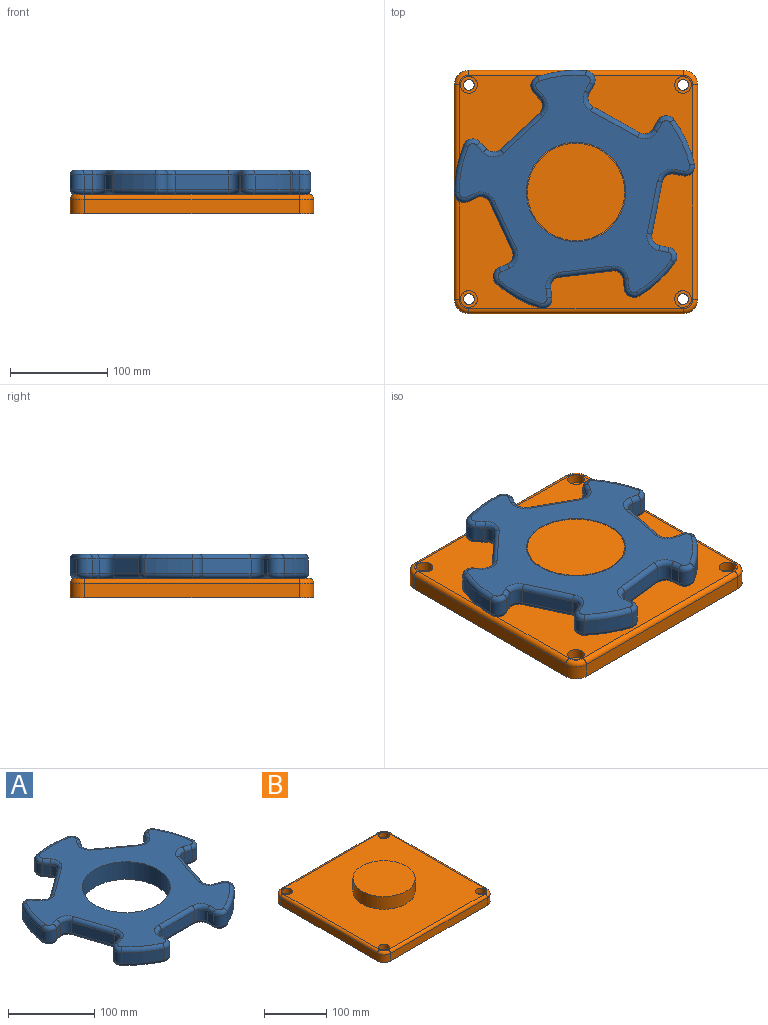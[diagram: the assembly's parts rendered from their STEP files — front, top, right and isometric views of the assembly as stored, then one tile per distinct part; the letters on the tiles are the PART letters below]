
ASSEMBLY  parts=2 mates=1
PART A: 123 faces, bbox 268.9x258.5x25 mm
  f0: plane 238.57x229.73mm, normal (0,0,1), area 21505.7mm2, adj f6,f83,f84,f85,f86,f87,f88,f89
  f1: plane 238.57x229.73mm, normal (0,0,-1), area 21505.7mm2, adj f6,f43,f44,f45,f46,f47,f48,f49
  f2: cylinder r=125mm len=47.82mm, axis (0,0,-1), area 759.5mm2, adj f34,f42,f74,f114
  f3: cylinder r=125mm len=50.29mm, axis (0,0,-1), area 759.5mm2, adj f27,f35,f75,f115
  f4: cylinder r=125mm len=47.82mm, axis (0,0,-1), area 759.5mm2, adj f20,f28,f59,f99
  f5: cylinder r=125mm len=40.68mm, axis (0,0,-1), area 759.5mm2, adj f13,f21,f43,f83
  f6: cylinder r=51mm len=102mm, axis (0,0,-1), area 8011.1mm2, adj f0,f1
  f7: cylinder r=125mm len=40.68mm, axis (0,0,-1), area 759.5mm2, adj f14,f41,f58,f98
  f8: plane 15x9.73mm, normal (-1,0,0), area 146mm2, adj f11,f14,f54,f94
  f9: plane 55x15mm, normal (0,-1,0), area 825mm2, adj f11,f12,f50,f90
  f10: plane 15x9.73mm, normal (1,0,0), area 146mm2, adj f12,f13,f46,f86
  f11: cylinder r=10mm len=15mm, axis (0,0,-1), area 235.6mm2, adj f8,f9,f52,f92
  f12: cylinder r=10mm len=15mm, axis (0,0,-1), area 235.6mm2, adj f9,f10,f48,f88
  f13: cylinder r=10mm len=15mm, axis (0,0,-1), area 299.5mm2, adj f5,f10,f44,f84
  f14: cylinder r=10mm len=15mm, axis (0,0,-1), area 299.5mm2, adj f7,f8,f56,f96
  f15: plane 15x9.26mm, normal (-0.31,0.95,0), area 146mm2, adj f18,f21,f47,f87
  f16: plane 52.31x17mm, normal (-0.95,-0.31,0), area 825mm2, adj f18,f19,f51,f91
  f17: plane 15x9.26mm, normal (0.31,-0.95,0), area 146mm2, adj f19,f20,f55,f95
  f18: cylinder r=10mm len=15mm, axis (0,0,-1), area 235.6mm2, adj f15,f16,f49,f89
  f19: cylinder r=10mm len=15mm, axis (0,0,-1), area 235.6mm2, adj f16,f17,f53,f93
  f20: cylinder r=10mm len=15mm, axis (0,0,-1), area 299.5mm2, adj f4,f17,f57,f97
  f21: cylinder r=10mm len=16.25mm, axis (0,0,-1), area 299.5mm2, adj f5,f15,f45,f85
  f22: plane 15x7.87mm, normal (0.81,0.59,0), area 146mm2, adj f25,f28,f63,f103
  f23: plane 44.5x32.33mm, normal (-0.59,0.81,0), area 825mm2, adj f25,f26,f67,f107
  f24: plane 15x7.87mm, normal (-0.81,-0.59,0), area 146mm2, adj f26,f27,f71,f111
  f25: cylinder r=10mm len=15mm, axis (0,0,-1), area 235.6mm2, adj f22,f23,f65,f105
  f26: cylinder r=10mm len=15mm, axis (0,0,-1), area 235.6mm2, adj f23,f24,f69,f109
  f27: cylinder r=10mm len=15.67mm, axis (0,0,-1), area 299.5mm2, adj f3,f24,f73,f113
  f28: cylinder r=10mm len=16.78mm, axis (0,0,-1), area 299.5mm2, adj f4,f22,f61,f101
  f29: plane 15x7.87mm, normal (0.81,-0.59,0), area 146mm2, adj f32,f35,f79,f119
  f30: plane 44.5x32.33mm, normal (0.59,0.81,0), area 825mm2, adj f32,f33,f82,f122
  f31: plane 15x7.87mm, normal (-0.81,0.59,0), area 146mm2, adj f33,f34,f78,f118
  f32: cylinder r=10mm len=15mm, axis (0,0,-1), area 235.6mm2, adj f29,f30,f81,f121
  f33: cylinder r=10mm len=15mm, axis (0,0,-1), area 235.6mm2, adj f30,f31,f80,f120
  f34: cylinder r=10mm len=16.78mm, axis (0,0,-1), area 299.5mm2, adj f2,f31,f76,f116
  f35: cylinder r=10mm len=15.67mm, axis (0,0,-1), area 299.5mm2, adj f3,f29,f77,f117
  f36: plane 15x9.26mm, normal (-0.31,-0.95,0), area 146mm2, adj f39,f42,f70,f110
  f37: plane 52.31x17mm, normal (0.95,-0.31,0), area 825mm2, adj f39,f40,f66,f106
  f38: plane 15x9.26mm, normal (0.31,0.95,0), area 146mm2, adj f40,f41,f62,f102
  f39: cylinder r=10mm len=15mm, axis (0,0,-1), area 235.6mm2, adj f36,f37,f68,f108
  f40: cylinder r=10mm len=15mm, axis (0,0,-1), area 235.6mm2, adj f37,f38,f64,f104
  f41: cylinder r=10mm len=16.25mm, axis (0,0,-1), area 299.5mm2, adj f7,f38,f60,f100
  f42: cylinder r=10mm len=15mm, axis (0,0,-1), area 299.5mm2, adj f2,f36,f72,f112
  f43: torus R=120mm, axis (0,0,1), area 391.9mm2, adj f1,f5,f44,f45
  f44: torus R=5mm, axis (0,0,1), area 128.3mm2, adj f1,f13,f43,f46
  f45: torus R=5mm, axis (0,0,1), area 128.3mm2, adj f1,f21,f43,f47
  f46: cylinder r=5mm len=9.73mm, axis (0,-1,0), area 76.4mm2, adj f1,f10,f44,f48
  f47: cylinder r=5mm len=10.8mm, axis (0.95,0.31,0), area 76.4mm2, adj f1,f15,f45,f49
  f48: torus R=15mm, axis (0,0,1), area 145.8mm2, adj f1,f12,f46,f50
  f49: torus R=15mm, axis (0,0,1), area 145.8mm2, adj f1,f18,f47,f51
  f50: cylinder r=5mm len=55mm, axis (-1,0,0), area 432mm2, adj f1,f9,f48,f52
  f51: cylinder r=5mm len=53.85mm, axis (-0.31,0.95,0), area 432mm2, adj f1,f16,f49,f53
  f52: torus R=15mm, axis (0,0,1), area 145.8mm2, adj f1,f11,f50,f54
  f53: torus R=15mm, axis (0,0,1), area 145.8mm2, adj f1,f19,f51,f55
  f54: cylinder r=5mm len=9.73mm, axis (0,1,0), area 76.4mm2, adj f1,f8,f52,f56
  f55: cylinder r=5mm len=10.8mm, axis (-0.95,-0.31,0), area 76.4mm2, adj f1,f17,f53,f57
  f56: torus R=5mm, axis (0,0,1), area 128.3mm2, adj f1,f14,f54,f58
  f57: torus R=5mm, axis (0,0,1), area 128.3mm2, adj f1,f20,f55,f59
  f58: torus R=120mm, axis (0,0,1), area 391.9mm2, adj f1,f7,f56,f60
  f59: torus R=120mm, axis (0,0,1), area 391.9mm2, adj f1,f4,f57,f61
  f60: torus R=5mm, axis (0,0,1), area 128.3mm2, adj f1,f41,f58,f62
  f61: torus R=5mm, axis (0,0,1), area 128.3mm2, adj f1,f28,f59,f63
  f62: cylinder r=5mm len=10.8mm, axis (0.95,-0.31,0), area 76.4mm2, adj f1,f38,f60,f64
  f63: cylinder r=5mm len=10.81mm, axis (0.59,-0.81,0), area 76.4mm2, adj f1,f22,f61,f65
  f64: torus R=15mm, axis (0,0,1), area 145.8mm2, adj f1,f40,f62,f66
  f65: torus R=15mm, axis (0,0,1), area 145.8mm2, adj f1,f25,f63,f67
  f66: cylinder r=5mm len=53.85mm, axis (-0.31,-0.95,0), area 432mm2, adj f1,f37,f64,f68
  f67: cylinder r=5mm len=47.44mm, axis (0.81,0.59,0), area 432mm2, adj f1,f23,f65,f69
  f68: torus R=15mm, axis (0,0,1), area 145.8mm2, adj f1,f39,f66,f70
  f69: torus R=15mm, axis (0,0,1), area 145.8mm2, adj f1,f26,f67,f71
  f70: cylinder r=5mm len=10.8mm, axis (-0.95,0.31,0), area 76.4mm2, adj f1,f36,f68,f72
  f71: cylinder r=5mm len=10.81mm, axis (-0.59,0.81,0), area 76.4mm2, adj f1,f24,f69,f73
  f72: torus R=5mm, axis (0,0,1), area 128.3mm2, adj f1,f42,f70,f74
  f73: torus R=5mm, axis (0,0,1), area 128.3mm2, adj f1,f27,f71,f75
  f74: torus R=120mm, axis (0,0,1), area 391.9mm2, adj f1,f2,f72,f76
  f75: torus R=120mm, axis (0,0,1), area 391.9mm2, adj f1,f3,f73,f77
  f76: torus R=5mm, axis (0,0,1), area 128.3mm2, adj f1,f34,f74,f78
  f77: torus R=5mm, axis (0,0,1), area 128.3mm2, adj f1,f35,f75,f79
  f78: cylinder r=5mm len=10.81mm, axis (0.59,0.81,0), area 76.4mm2, adj f1,f31,f76,f80
  f79: cylinder r=5mm len=10.81mm, axis (-0.59,-0.81,0), area 76.4mm2, adj f1,f29,f77,f81
  f80: torus R=15mm, axis (0,0,1), area 145.8mm2, adj f1,f33,f78,f82
  f81: torus R=15mm, axis (0,0,1), area 145.8mm2, adj f1,f32,f79,f82
  f82: cylinder r=5mm len=47.44mm, axis (0.81,-0.59,0), area 432mm2, adj f1,f30,f80,f81
  f83: torus R=120mm, axis (0,0,1), area 391.9mm2, adj f0,f5,f84,f85
  f84: torus R=5mm, axis (0,0,1), area 128.3mm2, adj f0,f13,f83,f86
  f85: torus R=5mm, axis (0,0,1), area 128.3mm2, adj f0,f21,f83,f87
  f86: cylinder r=5mm len=9.73mm, axis (0,1,0), area 76.4mm2, adj f0,f10,f84,f88
  f87: cylinder r=5mm len=10.8mm, axis (-0.95,-0.31,0), area 76.4mm2, adj f0,f15,f85,f89
  f88: torus R=15mm, axis (0,0,1), area 145.8mm2, adj f0,f12,f86,f90
  f89: torus R=15mm, axis (0,0,1), area 145.8mm2, adj f0,f18,f87,f91
  f90: cylinder r=5mm len=55mm, axis (1,0,0), area 432mm2, adj f0,f9,f88,f92
  f91: cylinder r=5mm len=53.85mm, axis (0.31,-0.95,0), area 432mm2, adj f0,f16,f89,f93
  f92: torus R=15mm, axis (0,0,1), area 145.8mm2, adj f0,f11,f90,f94
  f93: torus R=15mm, axis (0,0,1), area 145.8mm2, adj f0,f19,f91,f95
  f94: cylinder r=5mm len=9.73mm, axis (0,-1,0), area 76.4mm2, adj f0,f8,f92,f96
  f95: cylinder r=5mm len=10.8mm, axis (0.95,0.31,0), area 76.4mm2, adj f0,f17,f93,f97
  f96: torus R=5mm, axis (0,0,1), area 128.3mm2, adj f0,f14,f94,f98
  f97: torus R=5mm, axis (0,0,1), area 128.3mm2, adj f0,f20,f95,f99
  f98: torus R=120mm, axis (0,0,1), area 391.9mm2, adj f0,f7,f96,f100
  f99: torus R=120mm, axis (0,0,1), area 391.9mm2, adj f0,f4,f97,f101
  f100: torus R=5mm, axis (0,0,1), area 128.3mm2, adj f0,f41,f98,f102
  f101: torus R=5mm, axis (0,0,1), area 128.3mm2, adj f0,f28,f99,f103
  f102: cylinder r=5mm len=10.8mm, axis (-0.95,0.31,0), area 76.4mm2, adj f0,f38,f100,f104
  f103: cylinder r=5mm len=10.81mm, axis (-0.59,0.81,0), area 76.4mm2, adj f0,f22,f101,f105
  f104: torus R=15mm, axis (0,0,1), area 145.8mm2, adj f0,f40,f102,f106
  f105: torus R=15mm, axis (0,0,1), area 145.8mm2, adj f0,f25,f103,f107
  f106: cylinder r=5mm len=53.85mm, axis (0.31,0.95,0), area 432mm2, adj f0,f37,f104,f108
  f107: cylinder r=5mm len=47.44mm, axis (-0.81,-0.59,0), area 432mm2, adj f0,f23,f105,f109
  f108: torus R=15mm, axis (0,0,1), area 145.8mm2, adj f0,f39,f106,f110
  f109: torus R=15mm, axis (0,0,1), area 145.8mm2, adj f0,f26,f107,f111
  f110: cylinder r=5mm len=10.8mm, axis (0.95,-0.31,0), area 76.4mm2, adj f0,f36,f108,f112
  f111: cylinder r=5mm len=10.81mm, axis (0.59,-0.81,0), area 76.4mm2, adj f0,f24,f109,f113
  f112: torus R=5mm, axis (0,0,1), area 128.3mm2, adj f0,f42,f110,f114
  f113: torus R=5mm, axis (0,0,1), area 128.3mm2, adj f0,f27,f111,f115
  f114: torus R=120mm, axis (0,0,1), area 391.9mm2, adj f0,f2,f112,f116
  f115: torus R=120mm, axis (0,0,1), area 391.9mm2, adj f0,f3,f113,f117
  f116: torus R=5mm, axis (0,0,1), area 128.3mm2, adj f0,f34,f114,f118
  f117: torus R=5mm, axis (0,0,1), area 128.3mm2, adj f0,f35,f115,f119
  f118: cylinder r=5mm len=10.81mm, axis (-0.59,-0.81,0), area 76.4mm2, adj f0,f31,f116,f120
  f119: cylinder r=5mm len=10.81mm, axis (0.59,0.81,0), area 76.4mm2, adj f0,f29,f117,f121
  f120: torus R=15mm, axis (0,0,1), area 145.8mm2, adj f0,f33,f118,f122
  f121: torus R=15mm, axis (0,0,1), area 145.8mm2, adj f0,f32,f119,f122
  f122: cylinder r=5mm len=47.44mm, axis (-0.81,0.59,0), area 432mm2, adj f0,f30,f120,f121
PART B: 32 faces, bbox 252.5x252.5x45 mm
  f0: plane 220x15mm, normal (1,0,0), area 3300mm2, adj f5,f8,f11,f27
  f1: plane 220x15mm, normal (0,1,0), area 3300mm2, adj f5,f8,f9,f31
  f2: plane 220x15mm, normal (-1,0,0), area 3300mm2, adj f5,f9,f10,f28
  f3: plane 220x15mm, normal (0,-1,0), area 3300mm2, adj f5,f10,f11,f24
  f4: plane 240x240mm, normal (0,0,1), area 48725.4mm2, adj f6,f14,f17,f20,f23,f24,f25,f26
  f5: plane 250x250mm, normal (0,0,-1), area 61926.7mm2, adj f0,f1,f2,f3,f8,f9,f10,f11
  f6: cylinder r=50mm len=100mm, axis (0,0,-1), area 7854mm2, adj f4,f7
  f7: plane 100x100mm, normal (0,0,1), area 7854mm2, adj f6
  f8: cylinder r=15mm len=15mm, axis (0,0,-1), area 353.4mm2, adj f0,f1,f5,f29
  f9: cylinder r=15mm len=15mm, axis (0,0,1), area 353.4mm2, adj f1,f2,f5,f30
  f10: cylinder r=15mm len=15mm, axis (0,0,-1), area 353.4mm2, adj f2,f3,f5,f26
  f11: cylinder r=15mm len=15mm, axis (0,0,1), area 353.4mm2, adj f0,f3,f5,f25
  f12: cylinder r=5.5mm len=11mm, axis (0,0,1), area 345.6mm2, adj f5,f13
  f13: plane 17.25x17.25mm, normal (0,0,1), area 138.7mm2, adj f12,f14
  f14: cylinder r=8.62mm len=17.25mm, axis (0,0,1), area 541.9mm2, adj f4,f13
  f15: cylinder r=5.5mm len=11mm, axis (0,0,1), area 345.6mm2, adj f5,f16
  f16: plane 17.25x17.25mm, normal (0,0,1), area 138.7mm2, adj f15,f17
  f17: cylinder r=8.62mm len=17.25mm, axis (0,0,1), area 541.9mm2, adj f4,f16
  f18: cylinder r=5.5mm len=11mm, axis (0,0,1), area 345.6mm2, adj f5,f19
  f19: plane 17.25x17.25mm, normal (0,0,1), area 138.7mm2, adj f18,f20
  f20: cylinder r=8.62mm len=17.25mm, axis (0,0,1), area 541.9mm2, adj f4,f19
  f21: cylinder r=5.5mm len=11mm, axis (0,0,1), area 345.6mm2, adj f5,f22
  f22: plane 17.25x17.25mm, normal (0,0,1), area 138.7mm2, adj f21,f23
  f23: cylinder r=8.62mm len=17.25mm, axis (0,0,1), area 541.9mm2, adj f4,f22
  f24: cylinder r=5mm len=220mm, axis (-1,0,0), area 1727.9mm2, adj f3,f4,f25,f26
  f25: torus R=10mm, axis (0,0,1), area 162.6mm2, adj f4,f11,f24,f27
  f26: torus R=10mm, axis (0,0,1), area 162.6mm2, adj f4,f10,f24,f28
  f27: cylinder r=5mm len=220mm, axis (0,-1,0), area 1727.9mm2, adj f0,f4,f25,f29
  f28: cylinder r=5mm len=220mm, axis (0,1,0), area 1727.9mm2, adj f2,f4,f26,f30
  f29: torus R=10mm, axis (0,0,1), area 162.6mm2, adj f4,f8,f27,f31
  f30: torus R=10mm, axis (0,0,1), area 162.6mm2, adj f4,f9,f28,f31
  f31: cylinder r=5mm len=220mm, axis (1,0,0), area 1727.9mm2, adj f1,f4,f29,f30
PLACE A rot(axis=(0,0,-1),137.2deg) t=(0,0,0)mm
PLACE B at identity fixed
MATE revolute A.f2 <-> B.f6  axis (0,0,-1) through (0,0,32.5)mm
